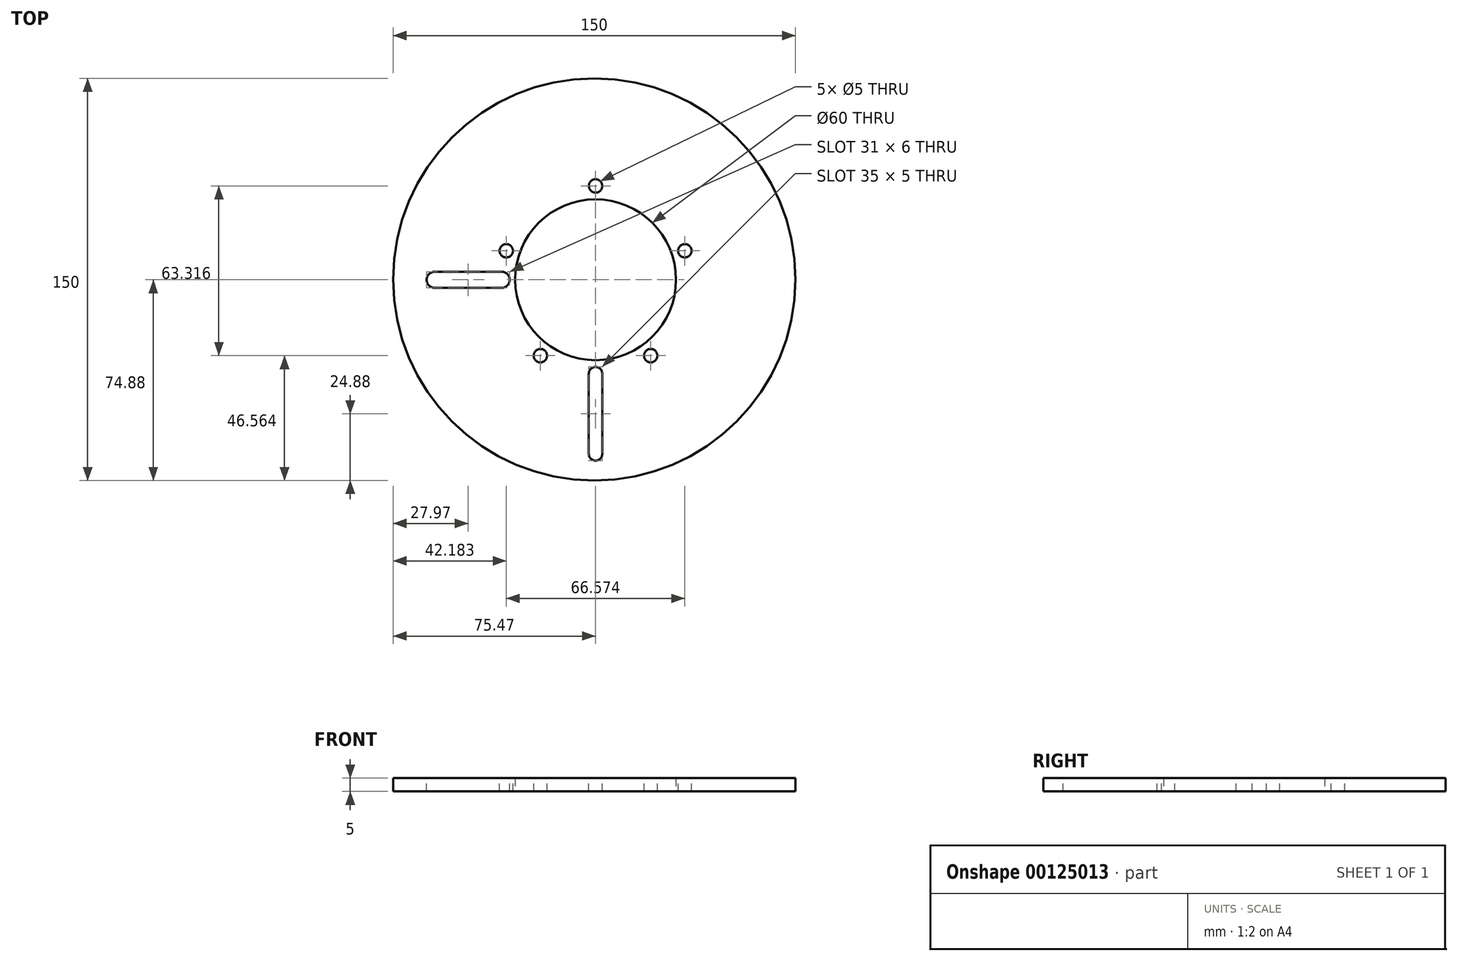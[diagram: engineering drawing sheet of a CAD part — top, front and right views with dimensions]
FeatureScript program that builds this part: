
annotation { "Feature Type Name" : "Feature", "Feature Type Description" : "" }
export const myFeature = defineFeature(function(context is Context, id is Id, definition is map)
    precondition{}
    {
        {
            var Q0;
            Q0=qCreatedBy(makeId("Top.planeOp"),FACE);
            var sketch = newSketch(context, id + "F0", { "sketchPlane" : qUnion([Q0])});
            skCircle(sketch, "E0", {"center": v(0, 0) * mm, "radius": 30 * mm});
            skCircle(sketch, "E1", {"center": v(-0.47, 0.12) * mm, "radius": 75 * mm});
            skSolve(sketch);
        }
        {
            var Q0;
            Q0=makeQuery(id+"F0.imprint","IMPRINT",FACE,{"disambiguationData":[TD([[makeQuery(id+"F0.imprint","IMPRINT",EDGE,{"derivedFrom":sQuery(id+"F0.wireOp",EDGE,"E0")}),-1.0]])]});
            extrude(context, id + "F1", {"entities" : qUnion([Q0]), "depth" : 5 * mm});
        }
        {
            var Q0;
            Q0=makeQuery(id+"F1.opExtrude","CAP_FACE",FACE,{"disambiguationData":[OSD([sQuery(id+"F0.wireOp",EDGE,"E0"),sQuery(id+"F0.wireOp",EDGE,"E1")])],"isStart":false});
            var sketch = newSketch(context, id + "F2", { "sketchPlane" : qUnion([Q0])});
            skCircle(sketch, "E2", {"center": v(0, 0) * mm, "radius": 35 * mm, "construction": true});
            skPoint(sketch, "E3", {"position": v(0, 35) * mm});
            skPoint(sketch, "E4.1.0", {"position": v(-33.29, 10.82) * mm});
            skPoint(sketch, "E4.2.0", {"position": v(-20.57, -28.32) * mm});
            skPoint(sketch, "E4.3.0", {"position": v(20.57, -28.32) * mm});
            skPoint(sketch, "E4.4.0", {"position": v(33.29, 10.82) * mm});
            skSolve(sketch);
        }
        {
            var Q0;
            Q0=sQuery(id+"F2.wireOp",VERTEX,"E3");
            var Q1;
            Q1=sQuery(id+"F2.wireOp",VERTEX,"E4.4.0");
            var Q2;
            Q2=sQuery(id+"F2.wireOp",VERTEX,"E4.3.0");
            var Q3;
            Q3=sQuery(id+"F2.wireOp",VERTEX,"E4.2.0");
            var Q4;
            Q4=sQuery(id+"F2.wireOp",VERTEX,"E4.1.0");
            var Q5;
            Q5=makeQuery(id+"F1.opExtrude","SWEPT_BODY",BODY,{"disambiguationData":[OSD([sQuery(id+"F0.wireOp",EDGE,"E0"),sQuery(id+"F0.wireOp",EDGE,"E1")])]});
            hole(context, id + "F3", {"style" : HoleStyle.SIMPLE, "endStyle" : HoleEndStyle.THROUGH, "holeDiameter" : 5 * mm, "locations" : qUnion([Q0, Q1, Q2, Q3, Q4]), "scope" : qUnion([Q5]), "isTappedThrough" : true});
        }
        {
            var Q0;
            Q0=makeQuery(id+"F1.opExtrude","CAP_FACE",FACE,{"disambiguationData":[OSD([sQuery(id+"F0.wireOp",EDGE,"E0"),sQuery(id+"F0.wireOp",EDGE,"E1")])],"isStart":false});
            var sketch = newSketch(context, id + "F4", { "sketchPlane" : qUnion([Q0])});
            skLineSegment(sketch, "E5.bottom", {"start": v(-2.5, -35) * mm, "end": v(2.5, -35) * mm, "construction": true});
            skLineSegment(sketch, "E5.top", {"start": v(-2.5, -65) * mm, "end": v(2.5, -65) * mm, "construction": true});
            skLineSegment(sketch, "E5.left", {"start": v(-2.5, -35) * mm, "end": v(-2.5, -65) * mm});
            skLineSegment(sketch, "E5.right", {"start": v(2.5, -35) * mm, "end": v(2.5, -65) * mm});
            skLineSegment(sketch, "E6", {"start": v(0, -35) * mm, "end": v(0, -65) * mm, "construction": true});
            skPoint(sketch, "E6.startSnap0", {"position": v(0, -35) * mm});
            skArc(sketch, "E7", {"start": v(2.5, -35) * mm, "mid": v(0, -32.5) * mm, "end": v(-2.5, -35) * mm});
            skArc(sketch, "E8", {"start": v(-2.5, -65) * mm, "mid": v(0, -67.5) * mm, "end": v(2.5, -65) * mm});
            skSolve(sketch);
        }
        {
            var Q0;
            Q0 = qSketchRegion(id + "F4", true);
            extrude(context, id + "F5", {"entities" : qUnion([Q0]), "operationType" : NewBodyOperationType.REMOVE, "endBound" : BoundingType.UP_TO_NEXT, "oppositeDirection" : true, "depth" : 25 * mm});
        }
        {
            var Q0;
            Q0=makeQuery(id+"F1.opExtrude","CAP_FACE",FACE,{"disambiguationData":[OSD([sQuery(id+"F0.wireOp",EDGE,"E0"),sQuery(id+"F0.wireOp",EDGE,"E1")])],"isStart":false});
            var sketch = newSketch(context, id + "F6", { "sketchPlane" : qUnion([Q0])});
            skLineSegment(sketch, "E9", {"start": v(-60, 0) * mm, "end": v(-35, 0) * mm});
            skArc(sketch, "E10.0.startCap", {"start": v(-60, -3) * mm, "mid": v(-63, 0) * mm, "end": v(-60, 3) * mm});
            skArc(sketch, "E10.0.endCap", {"start": v(-35, 3) * mm, "mid": v(-32, 0) * mm, "end": v(-35, -3) * mm});
            skLineSegment(sketch, "E10.0.left", {"start": v(-60, 3) * mm, "end": v(-35, 3) * mm});
            skLineSegment(sketch, "E10.0.right", {"start": v(-60, -3) * mm, "end": v(-35, -3) * mm});
            skSolve(sketch);
        }
        {
            var Q0;
            Q0 = qSketchRegion(id + "F6", true);
            extrude(context, id + "F7", {"entities" : qUnion([Q0]), "operationType" : NewBodyOperationType.REMOVE, "endBound" : BoundingType.UP_TO_NEXT, "oppositeDirection" : true, "depth" : 25 * mm});
        }
    });
